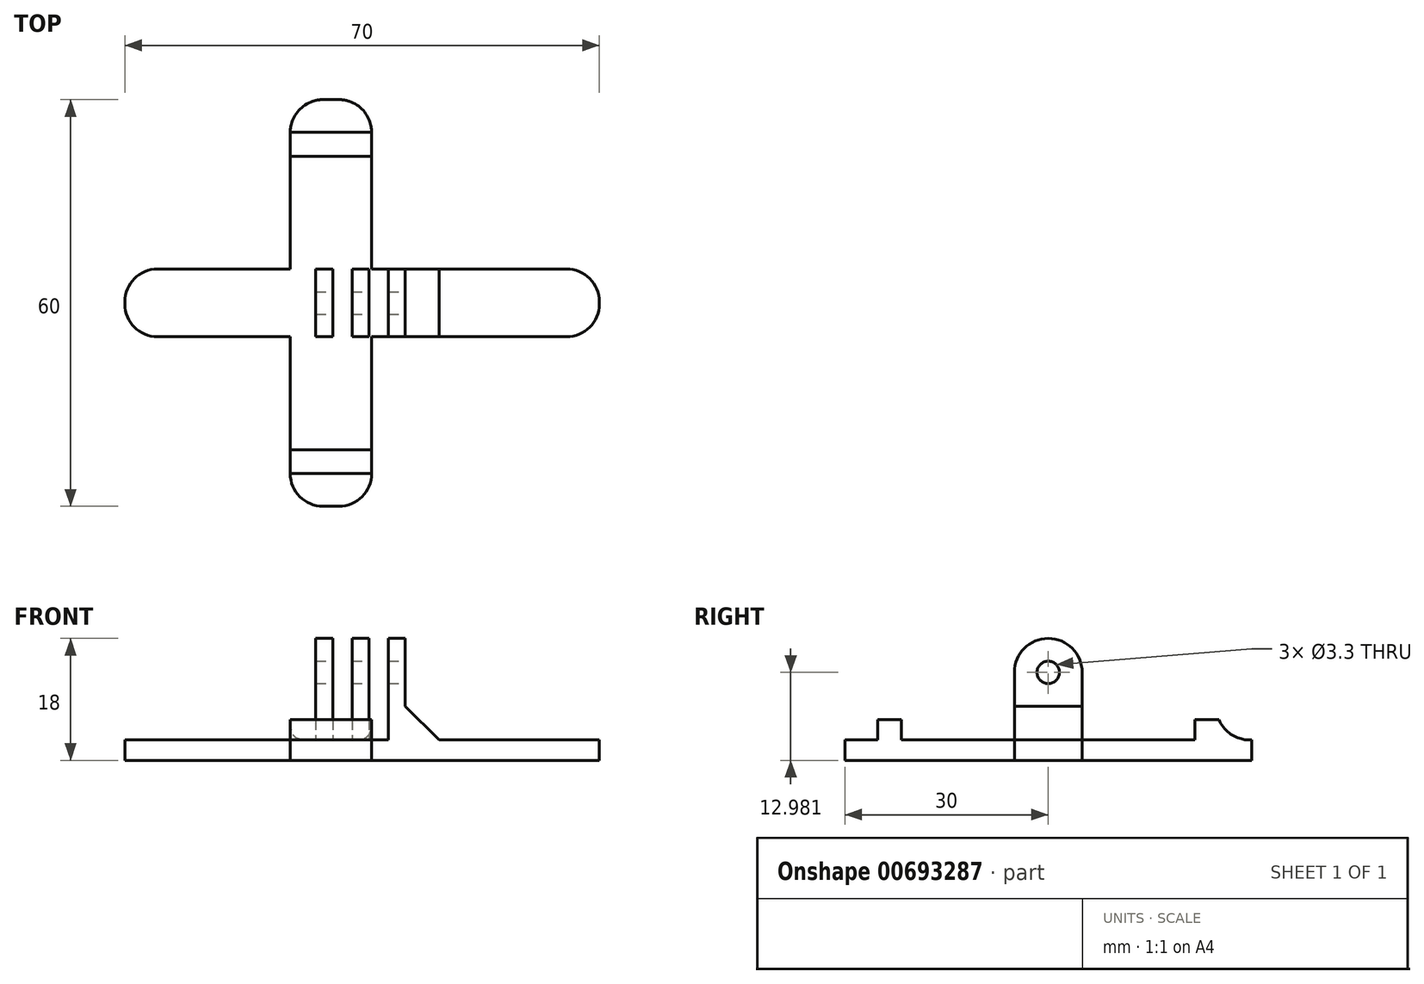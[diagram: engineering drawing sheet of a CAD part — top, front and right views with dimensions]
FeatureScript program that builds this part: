
annotation { "Feature Type Name" : "Feature", "Feature Type Description" : "" }
export const myFeature = defineFeature(function(context is Context, id is Id, definition is map)
    precondition{}
    {
        {
            var Q0;
            Q0=qCreatedBy(makeId("Top.planeOp"),FACE);
            var sketch = newSketch(context, id + "F0", { "sketchPlane" : qUnion([Q0])});
            skLineSegment(sketch, "E0.bottom", {"start": v(35, 5) * mm, "end": v(-35, 5) * mm});
            skLineSegment(sketch, "E0.top", {"start": v(35, -5) * mm, "end": v(-35, -5) * mm});
            skLineSegment(sketch, "E0.left", {"start": v(35, 5) * mm, "end": v(35, -5) * mm});
            skLineSegment(sketch, "E0.right", {"start": v(-35, 5) * mm, "end": v(-35, -5) * mm});
            skPoint(sketch, "E0.middle", {"position": v(0, 0) * mm});
            skLineSegment(sketch, "E1", {"start": v(-10.6, 5) * mm, "end": v(-10.6, 30) * mm});
            skLineSegment(sketch, "E2", {"start": v(-10.6, 30) * mm, "end": v(1.4, 30) * mm});
            skLineSegment(sketch, "E3", {"start": v(1.4, 30) * mm, "end": v(1.4, 5) * mm});
            skLineSegment(sketch, "E4.MirrorCS", {"start": v(-10.6, -5) * mm, "end": v(-10.6, -30) * mm});
            skLineSegment(sketch, "E5.MirrorCS", {"start": v(-10.6, -30) * mm, "end": v(1.4, -30) * mm});
            skLineSegment(sketch, "E6.MirrorCS", {"start": v(1.4, -30) * mm, "end": v(1.4, -5) * mm});
            skSolve(sketch);
        }
        {
            var Q0;
            Q0=qSketchRegion(id+"F0",true);
            extrude(context, id + "F1", {"entities" : qUnion([Q0]), "depth" : 3 * mm, "offsetDistance" : 25 * mm});
        }
        {
            var Q0;
            Q0=makeQuery(id+"F1.opExtrude","CAP_FACE",FACE,{"disambiguationData":[OSD([sQuery(id+"F0.wireOp",EDGE,"E0.bottom"),sQuery(id+"F0.wireOp",EDGE,"E0.top"),sQuery(id+"F0.wireOp",EDGE,"E0.left"),sQuery(id+"F0.wireOp",EDGE,"E0.right")])],"isStart":false});
            var sketch = newSketch(context, id + "F2", { "sketchPlane" : qUnion([Q0])});
            skLineSegment(sketch, "E7.bottom", {"start": v(6.38, 5) * mm, "end": v(6.38, -5) * mm});
            skLineSegment(sketch, "E7.top", {"start": v(3.88, 5) * mm, "end": v(3.88, -5) * mm});
            skLineSegment(sketch, "E7.left", {"start": v(6.38, 5) * mm, "end": v(3.88, 5) * mm});
            skLineSegment(sketch, "E7.right", {"start": v(6.38, -5) * mm, "end": v(3.88, -5) * mm});
            skLineSegment(sketch, "E8.direction1", {"start": v(3.88, 5) * mm, "end": v(3.88, -19.58) * mm, "construction": true});
            skLineSegment(sketch, "E9.0.1.0", {"start": v(5.54, 16.75) * mm, "end": v(23.22, -0.93) * mm, "construction": true});
            skLineSegment(sketch, "E9.0.1.1", {"start": v(1.03, 5) * mm, "end": v(1.03, -5) * mm});
            skLineSegment(sketch, "E9.0.1.2", {"start": v(-1.47, 5) * mm, "end": v(-1.47, -5) * mm});
            skLineSegment(sketch, "E9.0.1.3", {"start": v(1.03, 5) * mm, "end": v(-1.47, 5) * mm});
            skLineSegment(sketch, "E9.0.1.4", {"start": v(1.03, -5) * mm, "end": v(-1.47, -5) * mm});
            skLineSegment(sketch, "E9.0.2.0", {"start": v(1.76, 12.96) * mm, "end": v(19.44, -4.72) * mm, "construction": true});
            skLineSegment(sketch, "E9.0.2.1", {"start": v(-4.32, 5) * mm, "end": v(-4.32, -5) * mm});
            skLineSegment(sketch, "E9.0.2.2", {"start": v(-6.82, 5) * mm, "end": v(-6.82, -5) * mm});
            skLineSegment(sketch, "E9.0.2.3", {"start": v(-4.32, 5) * mm, "end": v(-6.82, 5) * mm});
            skLineSegment(sketch, "E9.0.2.4", {"start": v(-4.32, -5) * mm, "end": v(-6.82, -5) * mm});
            skLineSegment(sketch, "E9.direction2", {"start": v(3.88, 5) * mm, "end": v(-1.47, 5) * mm, "construction": true});
            skSolve(sketch);
        }
        {
            var Q0;
            Q0=makeQuery(id+"F2.imprint","IMPRINT",FACE,{"disambiguationData":[TD([[makeQuery(id+"F2.imprint","IMPRINT",EDGE,{"derivedFrom":sQuery(id+"F2.wireOp",EDGE,"E9.0.2.1")}),-1.0]])]});
            var Q1;
            Q1=makeQuery(id+"F2.imprint","IMPRINT",FACE,{"disambiguationData":[TD([[makeQuery(id+"F2.imprint","IMPRINT",EDGE,{"derivedFrom":sQuery(id+"F2.wireOp",EDGE,"E9.0.1.1")}),-1.0]])]});
            var Q2;
            Q2=makeQuery(id+"F2.imprint","IMPRINT",FACE,{"disambiguationData":[TD([[makeQuery(id+"F2.imprint","IMPRINT",EDGE,{"derivedFrom":sQuery(id+"F2.wireOp",EDGE,"E7.bottom")}),-1.0]])]});
            extrude(context, id + "F3", {"entities" : qUnion([Q0, Q1, Q2]), "operationType" : NewBodyOperationType.ADD, "depth" : 15 * mm, "offsetDistance" : 25 * mm});
        }
        {
            var Q0;
            Q0=makeQuery(id+"F3.opExtrude","SWEPT_FACE",FACE,{"disambiguationData":[OSD([sQuery(id+"F2.wireOp",EDGE,"E7.bottom")])]});
            var sketch = newSketch(context, id + "F4", { "sketchPlane" : qUnion([Q0])});
            skPoint(sketch, "E10", {"position": v(0, 12.98) * mm});
            skPoint(sketch, "E10.positionSnap0", {"position": v(0, 18) * mm});
            skSolve(sketch);
        }
        {
            var Q0;
            Q0=sQuery(id+"F4.wireOp",VERTEX,"E10");
            var Q1;
            Q1=makeQuery(id+"F1.opExtrude","SWEPT_BODY",BODY,{"disambiguationData":[OSD([sQuery(id+"F0.wireOp",EDGE,"E0.bottom"),sQuery(id+"F0.wireOp",EDGE,"E0.top"),sQuery(id+"F0.wireOp",EDGE,"E0.left"),sQuery(id+"F0.wireOp",EDGE,"E0.right")])]});
            hole(context, id + "F5", {"style" : HoleStyle.SIMPLE, "endStyle" : HoleEndStyle.THROUGH, "standardTappedOrClearance" : lookupTablePath({ "standard" : "ISO", "fit" : "Normal", "size" : "M3", "type" : "Clearance" }), "standardBlindInLast" : lookupTablePath({ "fit" : "Standard", "standard" : "ISO", "size" : "M3", "type" : "Clearance" }), "holeDiameter" : 3.3 * mm, "majorDiameter" : 5 * mm, "isTappedThrough" : true, "tappedDepth" : 12 * mm, "tapClearance" : 3, "startFromSketch" : true, "locations" : qUnion([Q0]), "scope" : qUnion([Q1])});
        }
        {
            var Q0;
            Q0=makeQuery(id+"F3.opExtrude","CAP_EDGE",EDGE,{"disambiguationData":[OSD([sQuery(id+"F2.wireOp",EDGE,"E7.left")])],"isStart":false});
            var Q1;
            Q1=makeQuery(id+"F3.opExtrude","CAP_EDGE",EDGE,{"disambiguationData":[OSD([sQuery(id+"F2.wireOp",EDGE,"E9.0.1.3")])],"isStart":false});
            var Q2;
            Q2=makeQuery(id+"F3.opExtrude","CAP_EDGE",EDGE,{"disambiguationData":[OSD([sQuery(id+"F2.wireOp",EDGE,"E9.0.2.3")])],"isStart":false});
            var Q3;
            Q3=makeQuery(id+"F3.opExtrude","CAP_EDGE",EDGE,{"disambiguationData":[OSD([sQuery(id+"F2.wireOp",EDGE,"E9.0.2.4")])],"isStart":false});
            var Q4;
            Q4=makeQuery(id+"F3.opExtrude","CAP_EDGE",EDGE,{"disambiguationData":[OSD([sQuery(id+"F2.wireOp",EDGE,"E9.0.1.4")])],"isStart":false});
            var Q5;
            Q5=makeQuery(id+"F3.opExtrude","CAP_EDGE",EDGE,{"disambiguationData":[OSD([sQuery(id+"F2.wireOp",EDGE,"E7.right")])],"isStart":false});
            fillet(context, id + "F6", {"entities" : qUnion([Q0, Q1, Q2, Q3, Q4, Q5]), "radius" : 5 * mm, "tangentPropagation" : true, "allowEdgeOverflow" : false});
        }
        {
            var Q0;
            Q0=makeQuery(id+"F1.opExtrude","SWEPT_EDGE",EDGE,{"disambiguationData":[OSD([sQuery(id+"F0.wireOp",EDGE,"E0.bottom"),sQuery(id+"F0.wireOp",EDGE,"E0.left")])]});
            var Q1;
            Q1=makeQuery(id+"F1.opExtrude","SWEPT_EDGE",EDGE,{"disambiguationData":[OSD([sQuery(id+"F0.wireOp",EDGE,"E0.top"),sQuery(id+"F0.wireOp",EDGE,"E0.left")])]});
            var Q2;
            Q2=makeQuery(id+"F1.opExtrude","SWEPT_EDGE",EDGE,{"disambiguationData":[OSD([sQuery(id+"F0.wireOp",EDGE,"E0.top"),sQuery(id+"F0.wireOp",EDGE,"E0.right")])]});
            var Q3;
            Q3=makeQuery(id+"F1.opExtrude","SWEPT_EDGE",EDGE,{"disambiguationData":[OSD([sQuery(id+"F0.wireOp",EDGE,"E0.bottom"),sQuery(id+"F0.wireOp",EDGE,"E0.right")])]});
            var Q4;
            Q4=makeQuery(id+"F1.opExtrude","SWEPT_EDGE",EDGE,{"disambiguationData":[OSD([sQuery(id+"F0.wireOp",EDGE,"E4.MirrorCS"),sQuery(id+"F0.wireOp",EDGE,"E5.MirrorCS")])]});
            var Q5;
            Q5=makeQuery(id+"F1.opExtrude","SWEPT_EDGE",EDGE,{"disambiguationData":[OSD([sQuery(id+"F0.wireOp",EDGE,"E5.MirrorCS"),sQuery(id+"F0.wireOp",EDGE,"E6.MirrorCS")])]});
            var Q6;
            Q6=makeQuery(id+"F1.opExtrude","SWEPT_EDGE",EDGE,{"disambiguationData":[OSD([sQuery(id+"F0.wireOp",EDGE,"E2"),sQuery(id+"F0.wireOp",EDGE,"E3")])]});
            var Q7;
            Q7=makeQuery(id+"F1.opExtrude","SWEPT_EDGE",EDGE,{"disambiguationData":[OSD([sQuery(id+"F0.wireOp",EDGE,"E1"),sQuery(id+"F0.wireOp",EDGE,"E2")])]});
            fillet(context, id + "F7", {"entities" : qUnion([Q0, Q1, Q2, Q3, Q4, Q5, Q6, Q7]), "radius" : 4.83 * mm, "tangentPropagation" : true, "allowEdgeOverflow" : false});
        }
        {
            var Q0;
            Q0=makeQuery(id+"F3.opExtrude","CAP_EDGE",EDGE,{"disambiguationData":[OSD([sQuery(id+"F2.wireOp",EDGE,"E7.bottom")])],"isStart":true});
            var Q1;
            Q1=makeQuery(id+"F3.opExtrude","CAP_EDGE",EDGE,{"disambiguationData":[OSD([sQuery(id+"F2.wireOp",EDGE,"E9.0.2.2")])],"isStart":true});
            chamfer(context, id + "F8", {"entities" : qUnion([Q0, Q1]), "width" : 5 * mm, "tangentPropagation" : true});
        }
        {
            var Q0;
            {var subQ0=sQuery(id+"F0.wireOp",EDGE,"E5.MirrorCS");var subQ1=sQuery(id+"F0.wireOp",EDGE,"E3");var subQ2=sQuery(id+"F0.wireOp",EDGE,"E2");var subQ3=sQuery(id+"F0.wireOp",EDGE,"E1");var subQ4=sQuery(id+"F0.wireOp",EDGE,"E0.left");var subQ5=sQuery(id+"F0.wireOp",EDGE,"E4.MirrorCS");var subQ6=sQuery(id+"F0.wireOp",EDGE,"E0.bottom");var subQ7=sQuery(id+"F0.wireOp",EDGE,"E0.right");var subQ8=sQuery(id+"F0.wireOp",EDGE,"E0.top");var subQ9=sQuery(id+"F0.wireOp",EDGE,"E6.MirrorCS");Q0=makeQuery(id+"F8.opChamfer","SPLIT",FACE,{"disambiguationData":[OD(0.0)],"derivedFrom":makeQuery(id+"F3.boolean.opBoolean","SPLIT",FACE,{"disambiguationData":[TD([makeQuery(id+"F1.opExtrude","SWEPT_FACE",FACE,{"disambiguationData":[OSD([subQ4])]})])],"derivedFrom":makeQuery(id+"F1.opExtrude","CAP_FACE",FACE,{"disambiguationData":[OSD([subQ6,subQ8,subQ4,subQ7,subQ3,subQ2,subQ1,subQ5,subQ0,subQ9])],"isStart":false})})});}
            var sketch = newSketch(context, id + "F9", { "sketchPlane" : qUnion([Q0])});
            skLineSegment(sketch, "E11.bottom", {"start": v(-10.6, 25.17) * mm, "end": v(1.4, 25.17) * mm});
            skLineSegment(sketch, "E11.top", {"start": v(-10.6, 21.65) * mm, "end": v(1.4, 21.65) * mm});
            skLineSegment(sketch, "E11.left", {"start": v(-10.6, 25.17) * mm, "end": v(-10.6, 21.65) * mm});
            skLineSegment(sketch, "E11.right", {"start": v(1.4, 25.17) * mm, "end": v(1.4, 21.65) * mm});
            skLineSegment(sketch, "E12.MirrorCS", {"start": v(-10.6, -25.17) * mm, "end": v(1.4, -25.17) * mm});
            skLineSegment(sketch, "E13.MirrorCS", {"start": v(-10.6, -21.65) * mm, "end": v(1.4, -21.65) * mm});
            skLineSegment(sketch, "E14.MirrorCS", {"start": v(1.4, -25.17) * mm, "end": v(1.4, -21.65) * mm});
            skLineSegment(sketch, "E15.MirrorCS", {"start": v(-10.6, -25.17) * mm, "end": v(-10.6, -21.65) * mm});
            skSolve(sketch);
        }
        {
            var Q0;
            Q0 = qSketchRegion(id + "F9", true);
            extrude(context, id + "F10", {"entities" : qUnion([Q0]), "operationType" : NewBodyOperationType.ADD, "depth" : 3 * mm, "offsetDistance" : 25 * mm});
        }
        {
            var Q0;
            Q0=makeQuery(id+"F10.opExtrude","CAP_EDGE",EDGE,{"disambiguationData":[OSD([sQuery(id+"F9.wireOp",EDGE,"E12.MirrorCS")])],"isStart":true});
            var Q1;
            Q1=makeQuery(id+"F10.opExtrude","CAP_EDGE",EDGE,{"disambiguationData":[OSD([sQuery(id+"F9.wireOp",EDGE,"E11.bottom")])],"isStart":true});
            fillet(context, id + "F11", {"entities" : qUnion([Q0, Q1]), "radius" : 5 * mm, "tangentPropagation" : true, "allowEdgeOverflow" : false});
        }
    });
